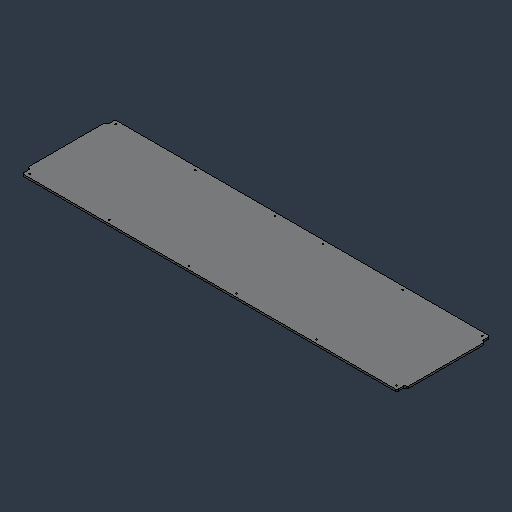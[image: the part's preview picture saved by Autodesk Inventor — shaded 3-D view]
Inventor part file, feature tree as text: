
AUTODESK INVENTOR PART (.ipt)
format: ipt  version: 2024.3 (Build 283343000, 343)  size: 100,864 bytes
history: native  units: mm (DEFAULTED — no unit token found)
features: fillet x1
ambient origin geometry x8: Origin, YZ Plane, XZ Plane, XY Plane, X Axis, Y Axis, Z Axis, Center Point
bodies: Solid1 (feature_tree)
feature tree (1):
  fillet  "Fillet1"  [1 undecoded]
note: 1 required parameter value undecoded (feature->parameter linkage not recoverable at this tier; creation-order binding heuristic only, values carry confidence <= 0.55)
